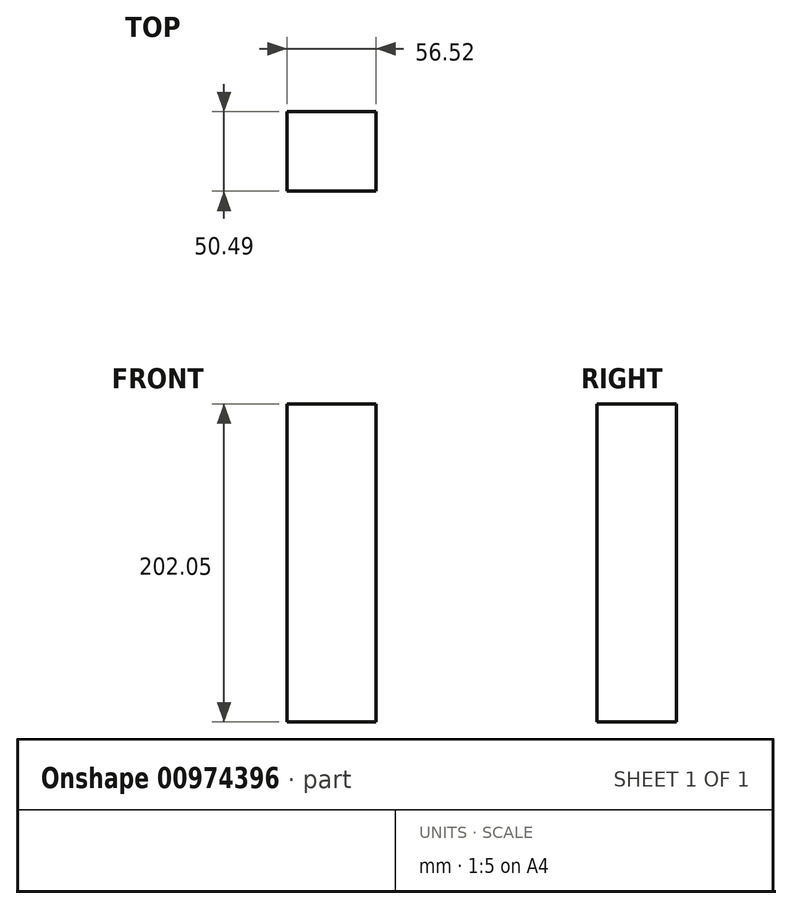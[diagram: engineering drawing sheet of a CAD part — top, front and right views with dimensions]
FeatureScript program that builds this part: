
annotation { "Feature Type Name" : "Feature", "Feature Type Description" : "" }
export const myFeature = defineFeature(function(context is Context, id is Id, definition is map)
    precondition{}
    {
        {
            var Q0;
            Q0=qCreatedBy(makeId("Top.planeOp"),FACE);
            var sketch = newSketch(context, id + "F0", { "sketchPlane" : qUnion([Q0])});
            skLineSegment(sketch, "E0.bottom", {"start": v(-26.07, 29.43) * mm, "end": v(30.46, 29.43) * mm});
            skLineSegment(sketch, "E0.top", {"start": v(-26.07, -21.06) * mm, "end": v(30.46, -21.06) * mm});
            skLineSegment(sketch, "E0.left", {"start": v(-26.07, 29.43) * mm, "end": v(-26.07, -21.06) * mm});
            skLineSegment(sketch, "E0.right", {"start": v(30.46, 29.43) * mm, "end": v(30.46, -21.06) * mm});
            skSolve(sketch);
        }
        {
            var Q0;
            Q0=makeQuery(id+"F0.imprint","IMPRINT",FACE,{"disambiguationData":[TD([[makeQuery(id+"F0.imprint","IMPRINT",EDGE,{"derivedFrom":sQuery(id+"F0.wireOp",EDGE,"E0.bottom")}),-1.0]])]});
            extrude(context, id + "F1", {"entities" : qUnion([Q0]), "depth" : 202.05 * mm, "offsetDistance" : 25.4 * mm});
        }
        {
            var Q0;
            Q0=makeQuery(id+"F1.opExtrude","SWEPT_BODY",BODY,{"disambiguationData":[OSD([sQuery(id+"F0.wireOp",EDGE,"E0.bottom"),sQuery(id+"F0.wireOp",EDGE,"E0.top"),sQuery(id+"F0.wireOp",EDGE,"E0.left"),sQuery(id+"F0.wireOp",EDGE,"E0.right")])]});
            var Q1;
            Q1=makeQuery(id+"F1.opExtrude","CAP_VERTEX",VERTEX,{"disambiguationData":[OSD([sQuery(id+"F0.wireOp",EDGE,"E0.top"),sQuery(id+"F0.wireOp",EDGE,"E0.left")])],"isStart":true});
            var Q2;
            Q2=makeQuery(id+"F1.opExtrude","SWEPT_EDGE",EDGE,{"disambiguationData":[OSD([sQuery(id+"F0.wireOp",EDGE,"E0.bottom"),sQuery(id+"F0.wireOp",EDGE,"E0.left")])]});
            transform(context, id + "F2", {"entities" : qUnion([Q0]), "transformType" : TransformType.TRANSLATION_ENTITY, "oppositeDirectionEntity" : false, "transformLine" : qUnion([Q1, Q2]), "makeCopy" : false});
        }
        {
            var Q0;
            Q0=makeQuery(id+"F1.opExtrude","SWEPT_BODY",BODY,{"disambiguationData":[OSD([sQuery(id+"F0.wireOp",EDGE,"E0.bottom"),sQuery(id+"F0.wireOp",EDGE,"E0.top"),sQuery(id+"F0.wireOp",EDGE,"E0.left"),sQuery(id+"F0.wireOp",EDGE,"E0.right")])]});
            var Q1;
            Q1=makeQuery(id+"F1.opExtrude","CAP_EDGE",EDGE,{"disambiguationData":[OSD([sQuery(id+"F0.wireOp",EDGE,"E0.bottom")])],"isStart":false});
            transform(context, id + "F3", {"entities" : qUnion([Q0]), "transformType" : TransformType.TRANSLATION_ENTITY, "oppositeDirectionEntity" : false, "transformLine" : qUnion([Q1]), "makeCopy" : false});
        }
    });
